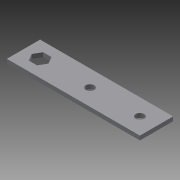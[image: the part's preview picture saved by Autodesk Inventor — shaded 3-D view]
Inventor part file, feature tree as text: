
AUTODESK INVENTOR PART (.ipt)
format: ipt  version: 2013 (Build 170138000, 138)  size: 117,760 bytes
history: native  units: in
note: dims shown in document units (in); Inventor stores cm internally (conversion verified against a paired STEP export)
features: extrude x5, sketch x5
ambient origin geometry x8: Origin, YZ Plane, XZ Plane, XY Plane, X Axis, Y Axis, Z Axis, Center Point
bodies: Solid1 (feature_tree)
feature tree (10):
  extrude  "Extrusion1"  Depth=1.0in
  extrude  "Extrusion2"  Depth=0.5in
  extrude  "Extrusion3"  Depth=1.5in
  extrude  "Extrusion4"  TaperAngle=0.0deg  [1 undecoded]
  extrude  "Extrusion5"  Depth=0.25in
  sketch  "Sketch1"  dims[d0=4.0in d1=1.0in]
  sketch  "Sketch2"  dims[d2=0.125in d3=0.0in d4=0.5in]
  sketch  "Sketch3"  dims[d5=0.125in d6=0.0in d7=1.5in]
  sketch  "Sketch4"  dims[d8=3.0in d9=0.0in]
  sketch  "Sketch5"  dims[d10=0.25in d11=0.25in d12=0.125in d13=0.0in d14=1.5in d15=1.0in d16=1.0in d17=0.0in d18=1.5in d19=0.0in d20=0.25in d21=1.5in d22=1.0in d23=0.125in d24=0.0in]
note: 1 required parameter value undecoded (feature->parameter linkage not recoverable at this tier; creation-order binding heuristic only, values carry confidence <= 0.55)
